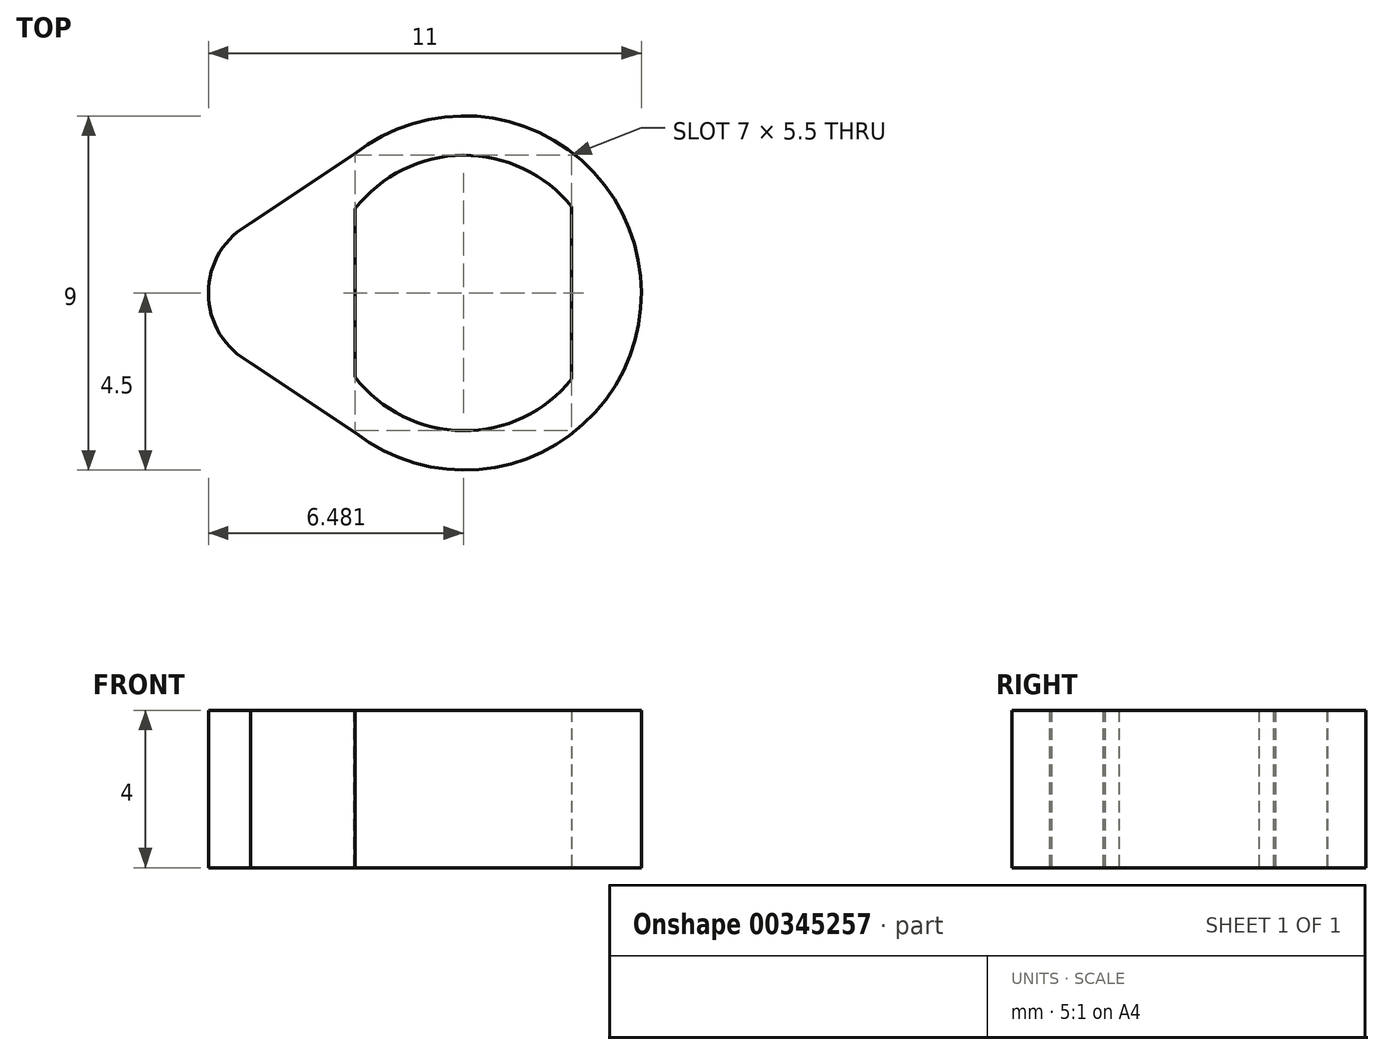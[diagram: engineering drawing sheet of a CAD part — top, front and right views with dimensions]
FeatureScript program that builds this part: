
annotation { "Feature Type Name" : "Feature", "Feature Type Description" : "" }
export const myFeature = defineFeature(function(context is Context, id is Id, definition is map)
    precondition{}
    {
        {
            var Q0;
            Q0=qCreatedBy(makeId("Top.planeOp"),FACE);
            var sketch = newSketch(context, id + "F0", { "sketchPlane" : qUnion([Q0])});
            skCircle(sketch, "E0", {"center": v(0, 0) * mm, "radius": 3.5 * mm});
            skCircle(sketch, "E1", {"center": v(0, 0) * mm, "radius": 4.5 * mm});
            skLineSegment(sketch, "E2", {"start": v(4.07, 6) * mm, "end": v(-4.6, 6) * mm, "construction": true});
            skCircle(sketch, "E3", {"center": v(-4.5, 0) * mm, "radius": 2 * mm});
            skLineSegment(sketch, "E4", {"start": v(2.73, 2.19) * mm, "end": v(2.73, -2.19) * mm});
            skLineSegment(sketch, "E5", {"start": v(-2.77, 2.14) * mm, "end": v(-2.77, -2.14) * mm});
            skLineSegment(sketch, "E6", {"start": v(-5.42, 1.77) * mm, "end": v(-2.8, 3.52) * mm});
            skLineSegment(sketch, "E7", {"start": v(-5.42, -1.77) * mm, "end": v(-2.77, -3.55) * mm});
            skSolve(sketch);
        }
        {
            var Q0;
            {var subQ0=sQuery(id+"F0.wireOp",EDGE,"E4");var subQ1=sQuery(id+"F0.wireOp",EDGE,"E0");var subQ2=makeQuery(id+"F0.imprint","INTERSECT",VERTEX,{"disambiguationData":[OD(0.0)],"derivedFrom":[subQ1,subQ0]});Q0=makeQuery(id+"F0.imprint","IMPRINT",FACE,{"disambiguationData":[TD([[makeQuery(id+"F0.imprint","IMPRINT",EDGE,{"disambiguationData":[TD([[subQ2,-1.0]])],"derivedFrom":subQ1}),-1.0]])]});}
            var Q1;
            {var subQ0=sQuery(id+"F0.wireOp",EDGE,"E5");Q1=makeQuery(id+"F0.imprint","IMPRINT",FACE,{"disambiguationData":[TD([[makeQuery(id+"F0.imprint","IMPRINT",EDGE,{"derivedFrom":subQ0}),-1.0]])]});}
            var Q2;
            {var subQ0=sQuery(id+"F0.wireOp",EDGE,"E4");Q2=makeQuery(id+"F0.imprint","IMPRINT",FACE,{"disambiguationData":[TD([[makeQuery(id+"F0.imprint","IMPRINT",EDGE,{"derivedFrom":subQ0}),1.0]])]});}
            var Q3;
            {var subQ0=sQuery(id+"F0.wireOp",EDGE,"E3");var subQ1=sQuery(id+"F0.wireOp",EDGE,"E1");var subQ2=makeQuery(id+"F0.imprint","INTERSECT",VERTEX,{"disambiguationData":[OD(0.0)],"derivedFrom":[subQ1,subQ0]});Q3=makeQuery(id+"F0.imprint","IMPRINT",FACE,{"disambiguationData":[TD([[makeQuery(id+"F0.imprint","IMPRINT",EDGE,{"disambiguationData":[TD([[subQ2,1.0]])],"derivedFrom":subQ1}),1.0]])]});}
            var Q4;
            {var subQ0=sQuery(id+"F0.wireOp",EDGE,"E3");var subQ1=sQuery(id+"F0.wireOp",EDGE,"E1");var subQ2=makeQuery(id+"F0.imprint","INTERSECT",VERTEX,{"disambiguationData":[OD(0.0)],"derivedFrom":[subQ1,subQ0]});Q4=makeQuery(id+"F0.imprint","IMPRINT",FACE,{"disambiguationData":[TD([[makeQuery(id+"F0.imprint","IMPRINT",EDGE,{"disambiguationData":[TD([[subQ2,1.0]])],"derivedFrom":subQ1}),-1.0]])]});}
            var Q5;
            {var subQ0=sQuery(id+"F0.wireOp",EDGE,"E3");var subQ1=sQuery(id+"F0.wireOp",EDGE,"E1");var subQ2=makeQuery(id+"F0.imprint","INTERSECT",VERTEX,{"disambiguationData":[OD(0.0)],"derivedFrom":[subQ1,subQ0]});Q5=makeQuery(id+"F0.imprint","IMPRINT",FACE,{"disambiguationData":[TD([[makeQuery(id+"F0.imprint","IMPRINT",EDGE,{"disambiguationData":[TD([[subQ2,-1.0]])],"derivedFrom":subQ1}),-1.0]])]});}
            var Q6;
            {var subQ0=sQuery(id+"F0.wireOp",EDGE,"E3");var subQ1=sQuery(id+"F0.wireOp",EDGE,"E0");var subQ2=makeQuery(id+"F0.imprint","INTERSECT",VERTEX,{"disambiguationData":[OD(0.0)],"derivedFrom":[subQ1,subQ0]});Q6=makeQuery(id+"F0.imprint","IMPRINT",FACE,{"disambiguationData":[TD([[makeQuery(id+"F0.imprint","IMPRINT",EDGE,{"disambiguationData":[TD([[subQ2,-1.0]])],"derivedFrom":subQ1}),-1.0]])]});}
            var Q7;
            {var subQ0=sQuery(id+"F0.wireOp",EDGE,"E3");var subQ1=sQuery(id+"F0.wireOp",EDGE,"E0");var subQ2=makeQuery(id+"F0.imprint","INTERSECT",VERTEX,{"disambiguationData":[OD(0.0)],"derivedFrom":[subQ1,subQ0]});Q7=makeQuery(id+"F0.imprint","IMPRINT",FACE,{"disambiguationData":[TD([[makeQuery(id+"F0.imprint","IMPRINT",EDGE,{"disambiguationData":[TD([[subQ2,-1.0]])],"derivedFrom":subQ1}),1.0]])]});}
            var Q8;
            {var subQ0=sQuery(id+"F0.wireOp",EDGE,"E7");Q8=makeQuery(id+"F0.imprint","IMPRINT",FACE,{"disambiguationData":[TD([[makeQuery(id+"F0.imprint","IMPRINT",EDGE,{"derivedFrom":subQ0}),1.0]])]});}
            extrude(context, id + "F1", {"entities" : qUnion([Q0, Q1, Q2, Q3, Q4, Q5, Q6, Q7, Q8]), "depth" : 4 * mm});
        }
    });
